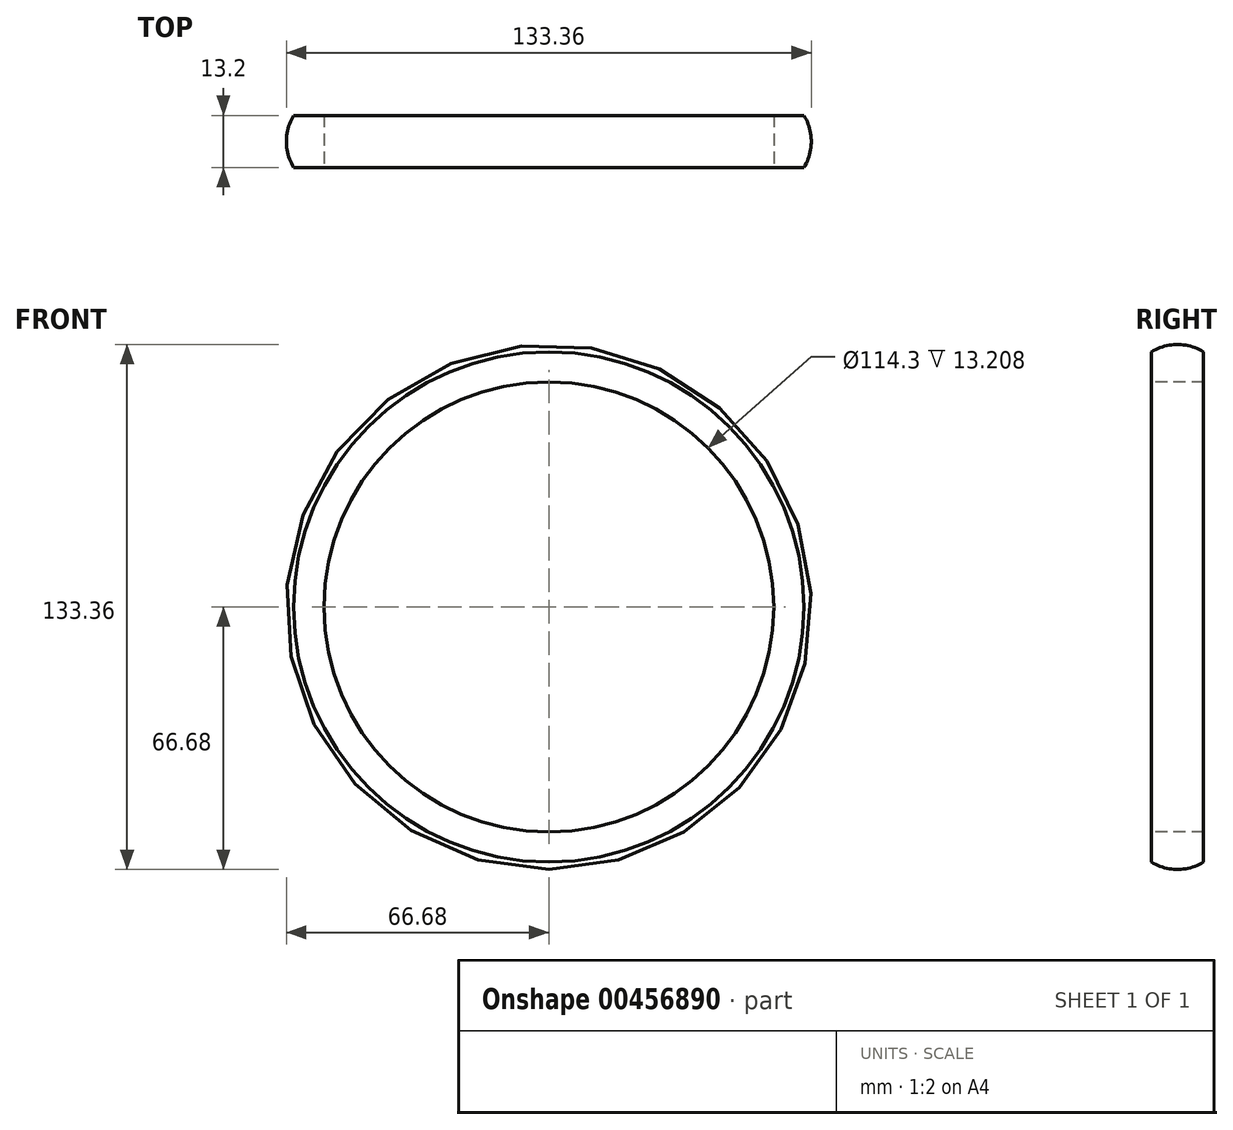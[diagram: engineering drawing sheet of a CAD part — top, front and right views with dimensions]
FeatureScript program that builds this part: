
annotation { "Feature Type Name" : "Feature", "Feature Type Description" : "" }
export const myFeature = defineFeature(function(context is Context, id is Id, definition is map)
    precondition{}
    {
        {
            var Q0;
            Q0=qCreatedBy(makeId("Right.planeOp"),FACE);
            var sketch = newSketch(context, id + "F0", { "sketchPlane" : qUnion([Q0])});
            skLineSegment(sketch, "E0", {"start": v(-6.6, 57.15) * mm, "end": v(-6.6, 64.82) * mm});
            skLineSegment(sketch, "E1", {"start": v(-6.6, 57.15) * mm, "end": v(6.6, 57.15) * mm});
            skLineSegment(sketch, "E2", {"start": v(6.6, 57.15) * mm, "end": v(6.6, 64.82) * mm});
            skArc(sketch, "E3", {"start": v(6.6, 64.82) * mm, "mid": v(0, 66.68) * mm, "end": v(-6.6, 64.82) * mm});
            skPoint(sketch, "E4", {"position": v(0, 57.15) * mm});
            skLineSegment(sketch, "E5", {"start": v(-21.47, 0) * mm, "end": v(22.38, 0) * mm, "construction": true});
            skSolve(sketch);
        }
        {
            var Q0;
            Q0=makeQuery(id+"F0.imprint","IMPRINT",FACE,{"disambiguationData":[TD([[makeQuery(id+"F0.imprint","IMPRINT",EDGE,{"derivedFrom":sQuery(id+"F0.wireOp",EDGE,"E0")}),-1.0]])]});
            var Q1;
            Q1=sQuery(id+"F0.wireOp",EDGE,"E5");
            revolve(context, id + "F1", {"entities" : qUnion([Q0]), "axis" : qUnion([Q1]), "revolveType" : RevolveType.FULL});
        }
    });
